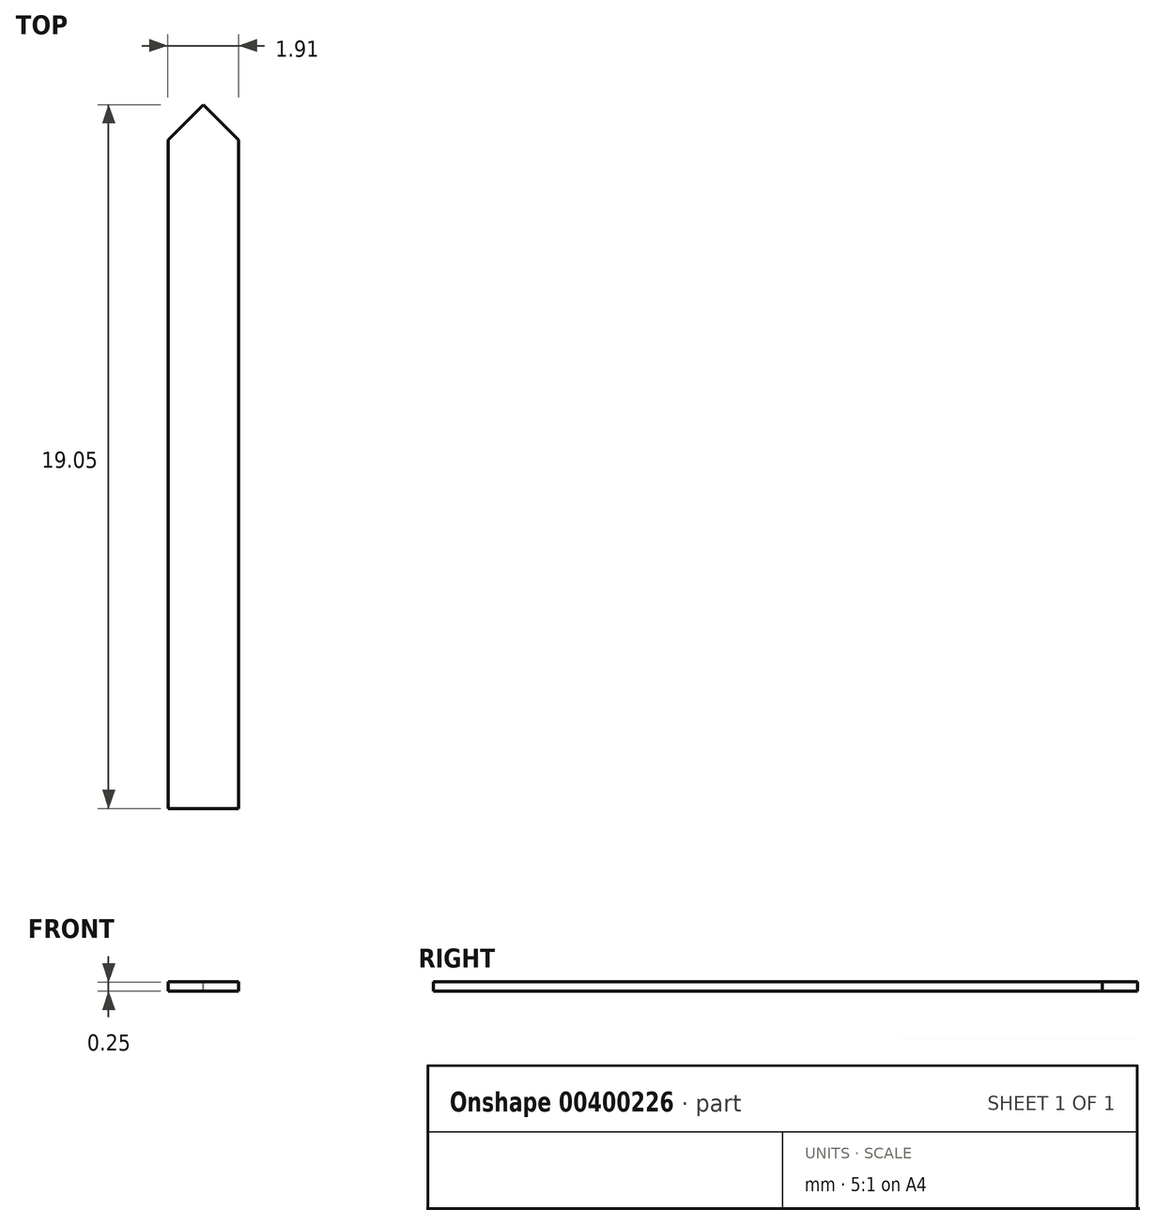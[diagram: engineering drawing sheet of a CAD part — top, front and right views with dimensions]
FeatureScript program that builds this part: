
annotation { "Feature Type Name" : "Feature", "Feature Type Description" : "" }
export const myFeature = defineFeature(function(context is Context, id is Id, definition is map)
    precondition{}
    {
        {
            var Q0;
            Q0=qCreatedBy(makeId("Top.planeOp"),FACE);
            var sketch = newSketch(context, id + "F0", { "sketchPlane" : qUnion([Q0])});
            skLineSegment(sketch, "E0.bottom", {"start": v(0, 0) * mm, "end": v(-1.9, 0) * mm});
            skLineSegment(sketch, "E0.top", {"start": v(0, 19.05) * mm, "end": v(-1.9, 19.05) * mm});
            skLineSegment(sketch, "E0.left", {"start": v(0, 0) * mm, "end": v(0, 19.05) * mm});
            skLineSegment(sketch, "E0.right", {"start": v(-1.9, 0) * mm, "end": v(-1.9, 19.05) * mm});
            skSolve(sketch);
        }
        {
            var Q0;
            Q0=makeQuery(id+"F0.imprint","IMPRINT",FACE,{"disambiguationData":[TD([[makeQuery(id+"F0.imprint","IMPRINT",EDGE,{"derivedFrom":sQuery(id+"F0.wireOp",EDGE,"E0.bottom")}),-1.0]])]});
            extrude(context, id + "F1", {"entities" : qUnion([Q0]), "depth" : 0.25 * mm});
        }
        {
            var Q0;
            Q0=makeQuery(id+"F1.opExtrude","SWEPT_EDGE",EDGE,{"disambiguationData":[OSD([sQuery(id+"F0.wireOp",EDGE,"E0.top"),sQuery(id+"F0.wireOp",EDGE,"E0.right")])]});
            chamfer(context, id + "F2", {"entities" : qUnion([Q0]), "width" : 0.95 * mm, "tangentPropagation" : true});
        }
        {
            var Q0;
            Q0=makeQuery(id+"F1.opExtrude","SWEPT_EDGE",EDGE,{"disambiguationData":[OSD([sQuery(id+"F0.wireOp",EDGE,"E0.top"),sQuery(id+"F0.wireOp",EDGE,"E0.left")])]});
            chamfer(context, id + "F3", {"entities" : qUnion([Q0]), "width" : 0.95 * mm, "tangentPropagation" : true});
        }
    });
